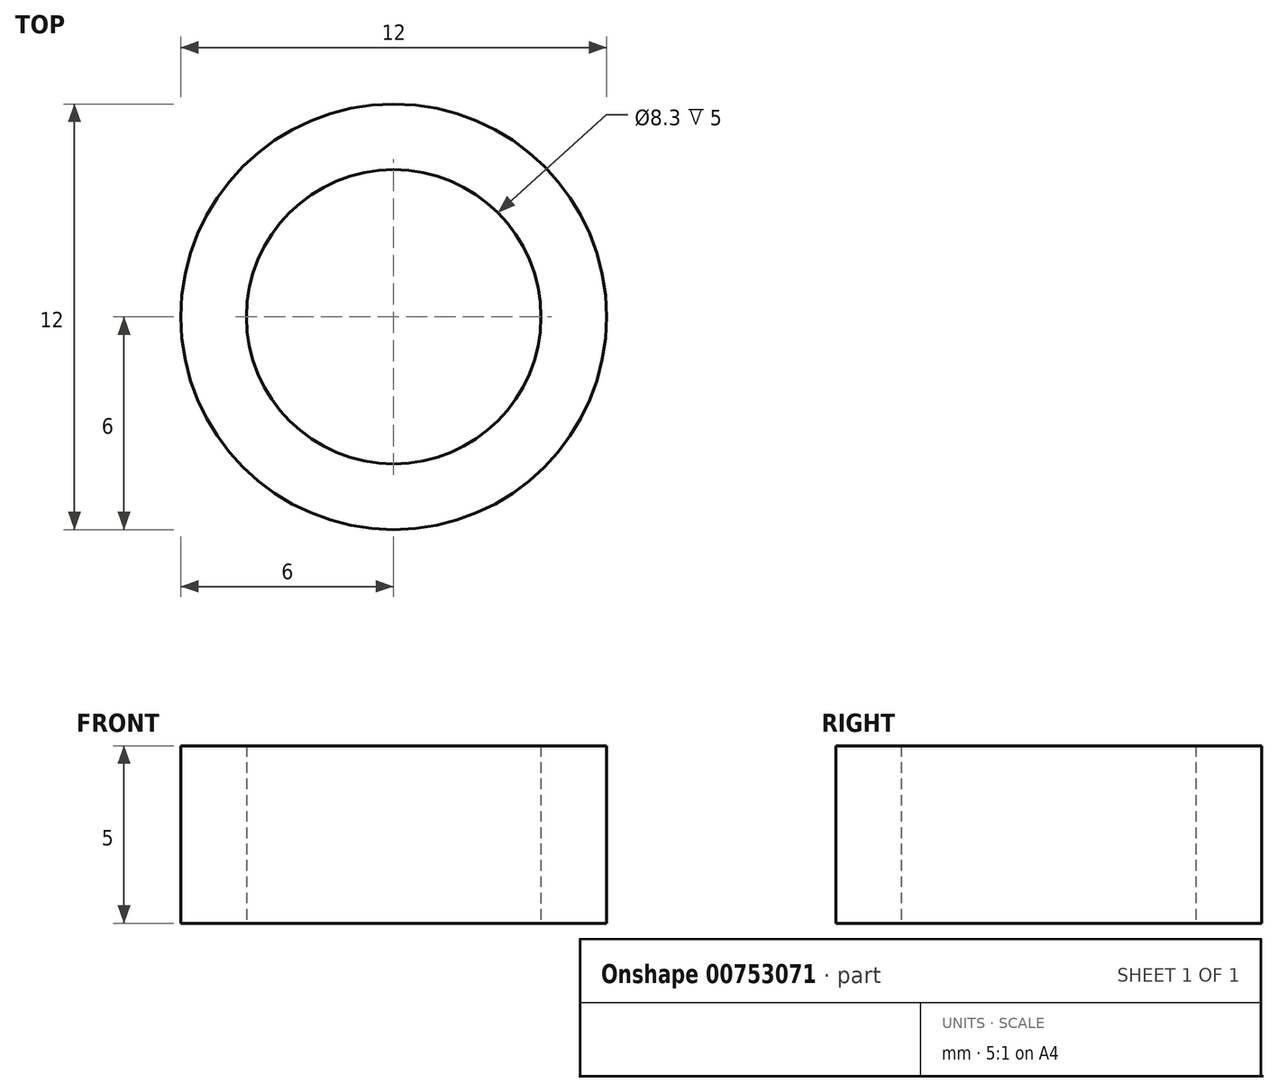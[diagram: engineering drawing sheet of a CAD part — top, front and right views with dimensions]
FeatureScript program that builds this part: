
annotation { "Feature Type Name" : "Feature", "Feature Type Description" : "" }
export const myFeature = defineFeature(function(context is Context, id is Id, definition is map)
    precondition{}
    {
        {
            var Q0;
            Q0=qCreatedBy(makeId("Top.planeOp"),FACE);
            var sketch = newSketch(context, id + "F0", { "sketchPlane" : qUnion([Q0])});
            skCircle(sketch, "E0", {"center": v(0, 0) * mm, "radius": 6 * mm});
            skCircle(sketch, "E1", {"center": v(0, 0) * mm, "radius": 4.15 * mm});
            skSolve(sketch);
        }
        {
            var Q0;
            Q0=qSketchRegion(id+"F0",true);
            extrude(context, id + "F1", {"entities" : qUnion([Q0]), "depth" : 5 * mm, "offsetDistance" : 25 * mm});
        }
    });
